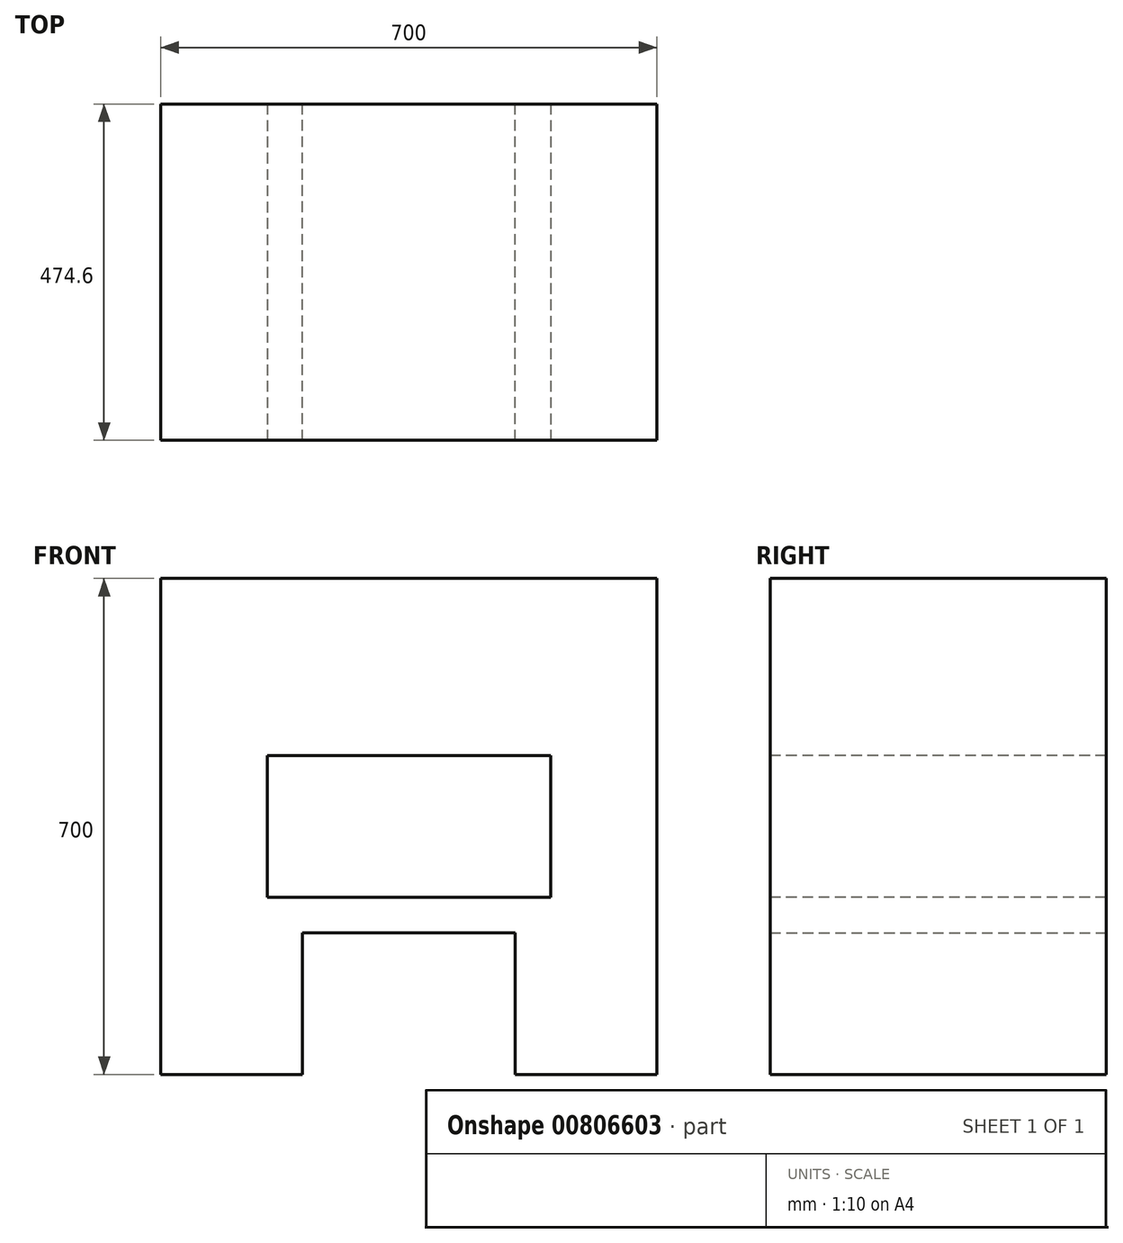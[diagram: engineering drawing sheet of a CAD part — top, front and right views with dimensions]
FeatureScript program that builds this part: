
annotation { "Feature Type Name" : "Feature", "Feature Type Description" : "" }
export const myFeature = defineFeature(function(context is Context, id is Id, definition is map)
    precondition{}
    {
        {
            var Q0;
            Q0=qCreatedBy(makeId("Front.planeOp"),FACE);
            var sketch = newSketch(context, id + "F0", { "sketchPlane" : qUnion([Q0])});
            skLineSegment(sketch, "E0.bottom", {"start": v(350, 350) * mm, "end": v(-350, 350) * mm});
            skLineSegment(sketch, "E0.top", {"start": v(350, -350) * mm, "end": v(-350, -350) * mm});
            skLineSegment(sketch, "E0.left", {"start": v(350, 350) * mm, "end": v(350, -350) * mm});
            skLineSegment(sketch, "E0.right", {"start": v(-350, 350) * mm, "end": v(-350, -350) * mm});
            skPoint(sketch, "E0.middle", {"position": v(0, 0) * mm});
            skLineSegment(sketch, "E1.bottom", {"start": v(150, -150) * mm, "end": v(-150, -150) * mm});
            skLineSegment(sketch, "E1.top", {"start": v(150, -550) * mm, "end": v(-150, -550) * mm});
            skLineSegment(sketch, "E1.left", {"start": v(150, -150) * mm, "end": v(150, -550) * mm});
            skLineSegment(sketch, "E1.right", {"start": v(-150, -150) * mm, "end": v(-150, -550) * mm});
            skPoint(sketch, "E1.middle", {"position": v(0, -350) * mm});
            skSolve(sketch);
        }
        {
            var Q0;
            Q0 = qSketchRegion(id + "FpA4MoCi6tA0OdT_0", true);
            var Q1;
            Q1=makeQuery(id+"F0.imprint","IMPRINT",FACE,{"disambiguationData":[TD([[makeQuery(id+"F0.imprint","IMPRINT",EDGE,{"derivedFrom":sQuery(id+"F0.wireOp",EDGE,"E0.bottom")}),1.0]])]});
            extrude(context, id + "F1", {"entities" : qUnion([Q0, Q1]), "depth" : 500 * mm, "offsetDistance" : 25.4 * mm});
        }
        {
            var Q0;
            {var subQ2=sQuery(id+"F0.wireOp",EDGE,"E1.top");var subQ9=makeQuery(id+"F0.imprint","IMPRINT",EDGE,{"derivedFrom":subQ2});Q0=makeQuery(id+"FpA4MoCi6tA0OdT_0.imprint","IMPRINT",FACE,{"disambiguationData":[TD([[makeQuery(id+"FpA4MoCi6tA0OdT_0.imprint","IMPRINT",EDGE,{"derivedFrom":subQ9}),-1.0]])]});}
            var sketch = newSketch(context, id + "F2", { "sketchPlane" : qUnion([Q0])});
            skSolve(sketch);
        }
        {
            var Q0;
            Q0 = qSketchRegion(id + "F2", true);
            var Q1;
            Q1=makeQuery(id+"F1.opExtrude","CAP_FACE",FACE,{"disambiguationData":[OSD([sQuery(id+"F0.wireOp",EDGE,"E0.bottom"),sQuery(id+"F0.wireOp",EDGE,"E0.top"),sQuery(id+"F0.wireOp",EDGE,"E0.left"),sQuery(id+"F0.wireOp",EDGE,"E0.right"),sQuery(id+"F0.wireOp",EDGE,"E1.bottom"),sQuery(id+"F0.wireOp",EDGE,"E1.left"),sQuery(id+"F0.wireOp",EDGE,"E1.right")])],"isStart":true});
            extrude(context, id + "F3", {"entities" : qUnion([Q0, Q1]), "operationType" : NewBodyOperationType.REMOVE, "oppositeDirection" : true, "depth" : 25.4 * mm, "offsetDistance" : 25.4 * mm});
        }
        {
            var Q0;
            Q0=makeQuery(id+"F1.opExtrude","CAP_FACE",FACE,{"disambiguationData":[OSD([sQuery(id+"F0.wireOp",EDGE,"E0.bottom"),sQuery(id+"F0.wireOp",EDGE,"E0.top"),sQuery(id+"F0.wireOp",EDGE,"E0.left"),sQuery(id+"F0.wireOp",EDGE,"E0.right"),sQuery(id+"F0.wireOp",EDGE,"E1.bottom"),sQuery(id+"F0.wireOp",EDGE,"E1.left"),sQuery(id+"F0.wireOp",EDGE,"E1.right")])],"isStart":false});
            var sketch = newSketch(context, id + "F4", { "sketchPlane" : qUnion([Q0])});
            skLineSegment(sketch, "E2.bottom", {"start": v(200, 100) * mm, "end": v(-200, 100) * mm});
            skLineSegment(sketch, "E2.top", {"start": v(200, -100) * mm, "end": v(-200, -100) * mm});
            skLineSegment(sketch, "E2.left", {"start": v(200, 100) * mm, "end": v(200, -100) * mm});
            skLineSegment(sketch, "E2.right", {"start": v(-200, 100) * mm, "end": v(-200, -100) * mm});
            skPoint(sketch, "E2.middle", {"position": v(0, 0) * mm});
            skSolve(sketch);
        }
        {
            var Q0;
            Q0=makeQuery(id+"F4.imprint","IMPRINT",FACE,{"disambiguationData":[TD([[makeQuery(id+"F4.imprint","IMPRINT",EDGE,{"derivedFrom":sQuery(id+"F4.wireOp",EDGE,"E2.bottom")}),1.0]])]});
            extrude(context, id + "F5", {"entities" : qUnion([Q0]), "operationType" : NewBodyOperationType.REMOVE, "endBound" : BoundingType.THROUGH_ALL, "oppositeDirection" : true, "depth" : 25.4 * mm, "offsetDistance" : 25.4 * mm});
        }
    });
